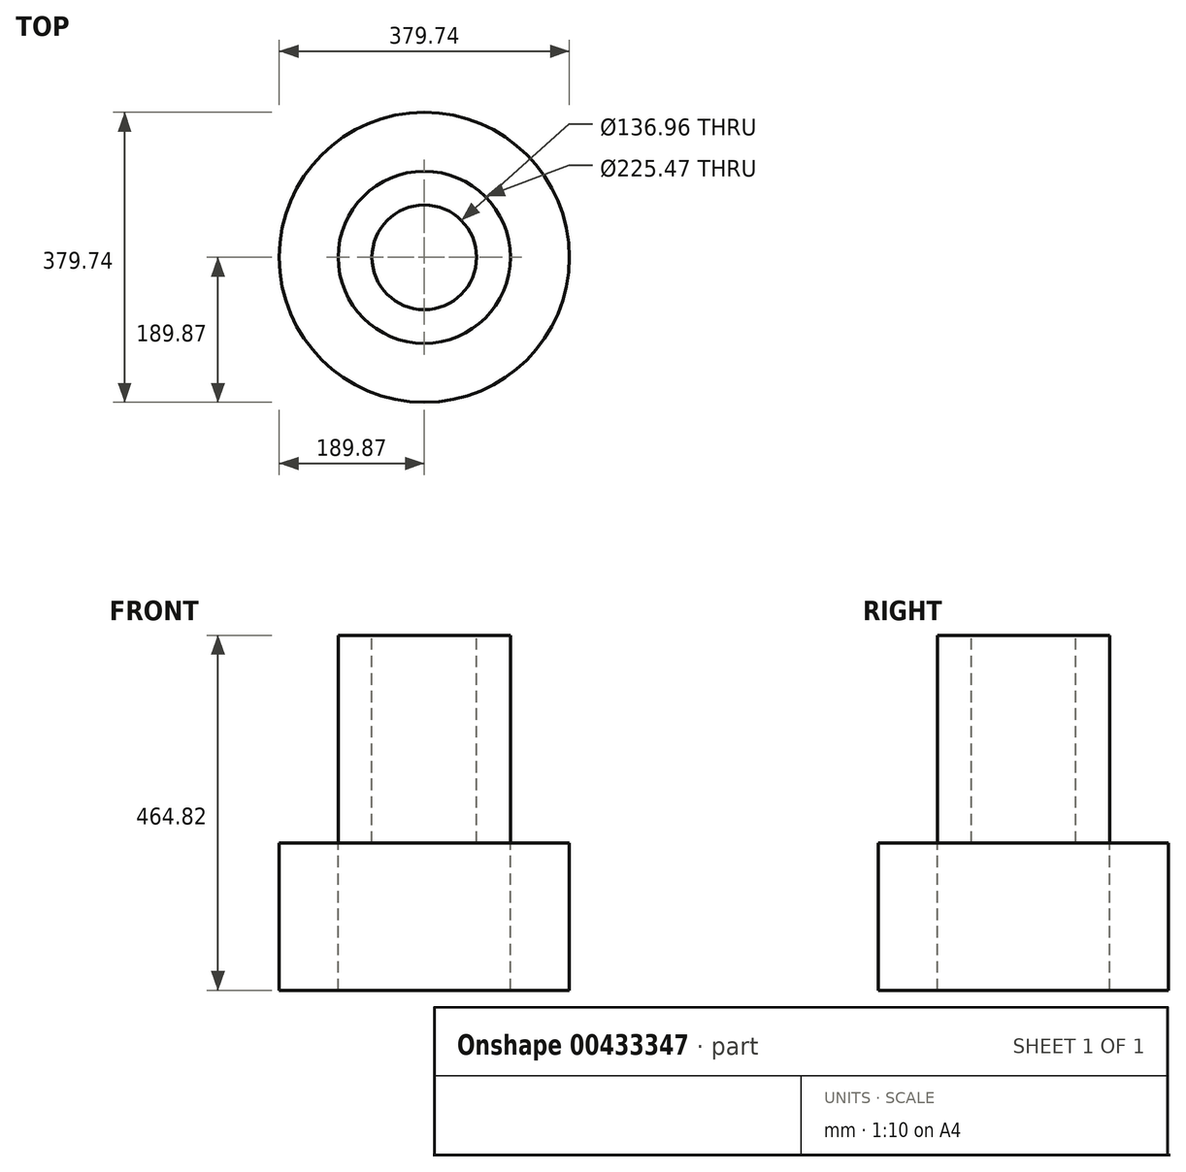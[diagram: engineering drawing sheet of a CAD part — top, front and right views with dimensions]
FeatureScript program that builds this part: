
annotation { "Feature Type Name" : "Feature", "Feature Type Description" : "" }
export const myFeature = defineFeature(function(context is Context, id is Id, definition is map)
    precondition{}
    {
        {
            var Q0;
            Q0=qCreatedBy(makeId("Top.planeOp"),FACE);
            var sketch = newSketch(context, id + "F0", { "sketchPlane" : qUnion([Q0])});
            skCircle(sketch, "E0", {"center": v(0, 0) * mm, "radius": 189.87 * mm});
            skSolve(sketch);
        }
        {
            var Q0;
            Q0=makeQuery(id+"F0.imprint","IMPRINT",FACE,{"disambiguationData":[TD([[makeQuery(id+"F0.imprint","IMPRINT",EDGE,{"derivedFrom":sQuery(id+"F0.wireOp",EDGE,"E0")}),1.0]])]});
            extrude(context, id + "F1", {"entities" : qUnion([Q0]), "oppositeDirection" : true, "depth" : 218.44 * mm});
        }
        {
            var Q0;
            Q0=makeQuery(id+"F1.opExtrude","CAP_FACE",FACE,{"disambiguationData":[OSD([sQuery(id+"F0.wireOp",EDGE,"E0")])],"isStart":true});
            var sketch = newSketch(context, id + "F2", { "sketchPlane" : qUnion([Q0])});
            skCircle(sketch, "E1", {"center": v(0, 0) * mm, "radius": 112.73 * mm});
            skSolve(sketch);
        }
        {
            var Q0;
            Q0=makeQuery(id+"F2.imprint","IMPRINT",FACE,{"disambiguationData":[TD([[makeQuery(id+"F2.imprint","IMPRINT",EDGE,{"derivedFrom":sQuery(id+"F2.wireOp",EDGE,"E1")}),1.0]])]});
            extrude(context, id + "F3", {"entities" : qUnion([Q0]), "operationType" : NewBodyOperationType.ADD, "depth" : 271.78 * mm});
        }
        {
            var Q0;
            Q0=makeQuery(id+"F3.opExtrude","CAP_FACE",FACE,{"disambiguationData":[OSD([sQuery(id+"F2.wireOp",EDGE,"E1")])],"isStart":false});
            var sketch = newSketch(context, id + "F4", { "sketchPlane" : qUnion([Q0])});
            skCircle(sketch, "E2", {"center": v(0, 0) * mm, "radius": 68.48 * mm});
            skSolve(sketch);
        }
        {
            var Q0;
            Q0=makeQuery(id+"F4.imprint","IMPRINT",FACE,{"disambiguationData":[TD([[makeQuery(id+"F4.imprint","IMPRINT",EDGE,{"derivedFrom":sQuery(id+"F4.wireOp",EDGE,"E2")}),1.0]])]});
            extrude(context, id + "F5", {"entities" : qUnion([Q0]), "operationType" : NewBodyOperationType.ADD, "depth" : 322.58 * mm});
        }
        {
            var Q0;
            Q0 = qSketchRegion(id + "F4", true);
            var Q1;
            Q1 = qSketchRegion(id + "F2", true);
            extrude(context, id + "F6", {"entities" : qUnion([Q0, Q1]), "operationType" : NewBodyOperationType.REMOVE, "oppositeDirection" : true, "depth" : 360.68 * mm});
        }
        {
            var Q0;
            Q0=makeQuery(id+"F5.opExtrude","CAP_FACE",FACE,{"disambiguationData":[OSD([sQuery(id+"F4.wireOp",EDGE,"E2")])],"isStart":false});
            extrude(context, id + "F7", {"entities" : qUnion([Q0]), "operationType" : NewBodyOperationType.REMOVE, "oppositeDirection" : true, "depth" : 1069.34 * mm});
        }
        {
            var Q0;
            Q0=makeQuery(id+"F1.opExtrude","CAP_FACE",FACE,{"disambiguationData":[OSD([sQuery(id+"F0.wireOp",EDGE,"E0")])],"isStart":false});
            extrude(context, id + "F8", {"entities" : qUnion([Q0]), "operationType" : NewBodyOperationType.REMOVE, "oppositeDirection" : true, "depth" : 25.4 * mm});
        }
    });
